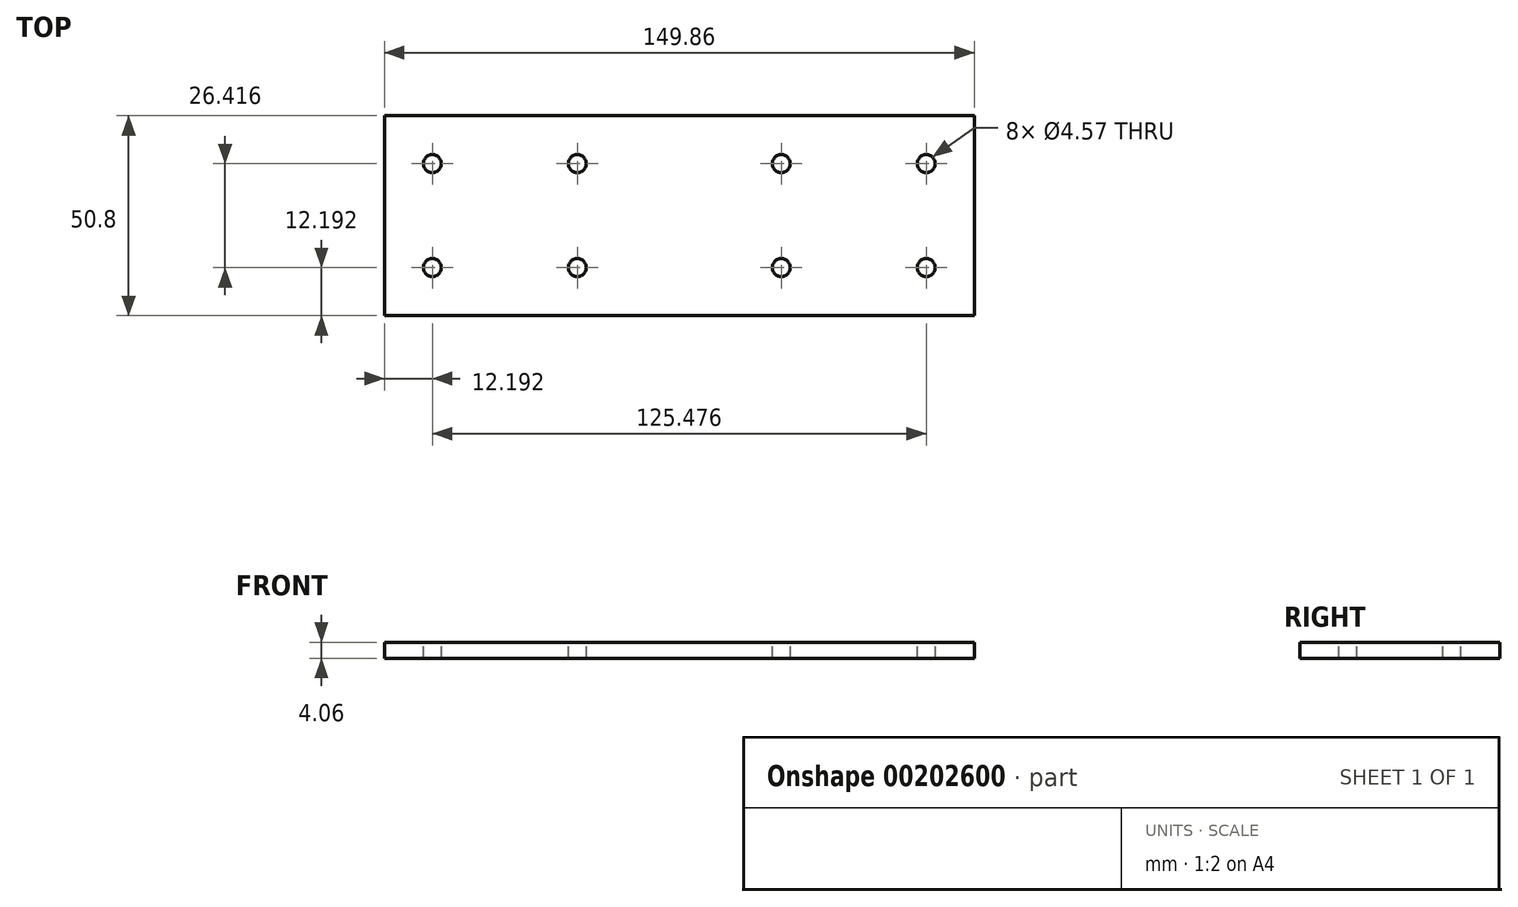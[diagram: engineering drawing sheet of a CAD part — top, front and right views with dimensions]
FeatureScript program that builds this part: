
annotation { "Feature Type Name" : "Feature", "Feature Type Description" : "" }
export const myFeature = defineFeature(function(context is Context, id is Id, definition is map)
    precondition{}
    {
        {
            var Q0;
            Q0=qCreatedBy(makeId("Top.planeOp"),FACE);
            var sketch = newSketch(context, id + "F0", { "sketchPlane" : qUnion([Q0])});
            skLineSegment(sketch, "E0.bottom", {"start": v(-74.93, 25.4) * mm, "end": v(74.93, 25.4) * mm});
            skLineSegment(sketch, "E0.top", {"start": v(-74.93, -25.4) * mm, "end": v(74.93, -25.4) * mm});
            skLineSegment(sketch, "E0.left", {"start": v(-74.93, 25.4) * mm, "end": v(-74.93, -25.4) * mm});
            skLineSegment(sketch, "E0.right", {"start": v(74.93, 25.4) * mm, "end": v(74.93, -25.4) * mm});
            skSolve(sketch);
        }
        {
            var Q0;
            Q0=makeQuery(id+"F0.imprint","IMPRINT",FACE,{"disambiguationData":[TD([[makeQuery(id+"F0.imprint","IMPRINT",EDGE,{"derivedFrom":sQuery(id+"F0.wireOp",EDGE,"E0.bottom")}),-1.0]])]});
            extrude(context, id + "F1", {"entities" : qUnion([Q0]), "depth" : 4.06 * mm});
        }
        {
            var Q0;
            Q0=makeQuery(id+"F1.opExtrude","CAP_FACE",FACE,{"disambiguationData":[OSD([sQuery(id+"F0.wireOp",EDGE,"E0.bottom"),sQuery(id+"F0.wireOp",EDGE,"E0.top"),sQuery(id+"F0.wireOp",EDGE,"E0.left"),sQuery(id+"F0.wireOp",EDGE,"E0.right")])],"isStart":false});
            var sketch = newSketch(context, id + "F2", { "sketchPlane" : qUnion([Q0])});
            skCircle(sketch, "E1", {"center": v(-62.74, 13.2) * mm, "radius": 2.29 * mm});
            skCircle(sketch, "E2", {"center": v(-25.9, 13.2) * mm, "radius": 2.29 * mm});
            skCircle(sketch, "E3", {"center": v(-62.74, -13.2) * mm, "radius": 2.29 * mm});
            skCircle(sketch, "E4", {"center": v(-25.9, -13.2) * mm, "radius": 2.29 * mm});
            skCircle(sketch, "E5", {"center": v(62.74, 13.2) * mm, "radius": 2.29 * mm});
            skCircle(sketch, "E6", {"center": v(25.9, 13.2) * mm, "radius": 2.29 * mm});
            skCircle(sketch, "E7", {"center": v(25.9, -13.2) * mm, "radius": 2.29 * mm});
            skCircle(sketch, "E8", {"center": v(62.74, -13.2) * mm, "radius": 2.29 * mm});
            skSolve(sketch);
        }
        {
            var Q0;
            Q0=sQuery(id+"F2.wireOp",VERTEX,"E1.center");
            var Q1;
            Q1=sQuery(id+"F2.wireOp",VERTEX,"E2.center");
            var Q2;
            Q2=sQuery(id+"F2.wireOp",VERTEX,"E4.center");
            var Q3;
            Q3=sQuery(id+"F2.wireOp",VERTEX,"E3.center");
            var Q4;
            Q4=sQuery(id+"F2.wireOp",VERTEX,"E6.center");
            var Q5;
            Q5=sQuery(id+"F2.wireOp",VERTEX,"E5.center");
            var Q6;
            Q6=sQuery(id+"F2.wireOp",VERTEX,"E8.center");
            var Q7;
            Q7=sQuery(id+"F2.wireOp",VERTEX,"E7.center");
            var Q8;
            Q8=makeQuery(id+"F1.opExtrude","SWEPT_BODY",BODY,{"disambiguationData":[OSD([sQuery(id+"F0.wireOp",EDGE,"E0.bottom"),sQuery(id+"F0.wireOp",EDGE,"E0.top"),sQuery(id+"F0.wireOp",EDGE,"E0.left"),sQuery(id+"F0.wireOp",EDGE,"E0.right")])]});
            hole(context, id + "F3", {"style" : HoleStyle.SIMPLE, "endStyle" : HoleEndStyle.THROUGH, "holeDiameter" : 4.57 * mm, "locations" : qUnion([Q0, Q1, Q2, Q3, Q4, Q5, Q6, Q7]), "scope" : qUnion([Q8]), "isTappedThrough" : true});
        }
    });
